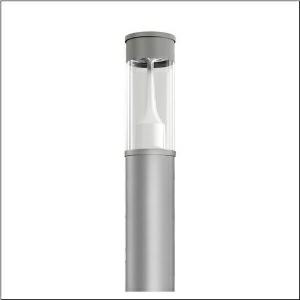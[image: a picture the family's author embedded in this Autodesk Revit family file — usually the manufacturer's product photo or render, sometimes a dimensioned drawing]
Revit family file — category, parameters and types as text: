
# Revit family: city-light_400_iq___p1_0a_5xa5305nf14hp_4342
name_source: partatom
category: Lighting Fixtures
units: mm (PartAtom-declared; Revit-internal decimal feet)

## family parameters
Cut with Voids When Loaded = No
Host = Face
Light Source = No
Part Type = Normal
Room Calculation Point = No
Round Connector Dimension = Use Diameter
Shared = No

## types (1)
- --- (1 x LED, 4210 lm, 33.6 W, 2700K)
    Apparent Load = 34 VA
    CIE Flux Codes = 31 62 91 95 100
    Color Rendering = 70
    Color Temperature = 2700K
    Default Elevation = 1800 mm
    Description = City-Light 400 iQ, light pillar, Module 540 iQ-SR, primary light control with 3 zone facetted reflector, of plastic, silver coated, highly specular, structured, primary optical cover: cover, of PMMA, transparent, partly coated, light distribution: P1.0a, primary light characteristic: strongly asymmetric, LED, High Power LED, rated luminous flux: 4.210lm, luminous efficacy: 125lm/W, light colour: 727, colour temperature: 2700K, control gear: iQ Street-Remote, control: pre-setting: logarithmic dimming characteristic, Street-Remote, Auto-Match, Temp-Guard, Lumen-Switch, Night-Set, Smart-Wire, Light-Fading, Desk-Remote (wireless, voltage-free reading and setting of iQ features in the workshop via application-optimized NFC function/RFID function), optimised constant luminous flux control (CLO 2.0), with terminal, 6-pole, max. 2.5mm², mains connection: 230..240V, AC, 50/60Hz, start of lifetime: 34W, end of service life: 36W, reduction: 15W, luminaire housing, cylindrical, of extruded aluminium section, coated, Siteco® metallic grey (DB 702S), length: 4.694mm, diameter: 200mm, Module 540 iQ-SR, traffic white (RAL 9016), equipment: Power, protection rating (complete): IP65, insulation class (complete): insulation class II (safety insulation), certification: CE, ENEC, VDE, packaging unit: 1 piece

Light Distribution: P1.0a
    Height = 500 mm
    Lamp = 1 x LED
    Lamp Light Flux = 4210 lm
    Lamp Power = 33.6 W
    Lamp count = 1
    Length = 200 mm  [stored 0.656168 ft]
    Luminous efficacy = 125 lm/W
    Manufacturer = Siteco
    ModVariant = No
    Model = 5XA5305NF14HP
    Mounting Place = Floor
    Mounting Type = Freestanding
    Number of Poles = 1
    OnlyDefault = Yes
    Power Factor = 1
    Product Name = City-Light 400 iQ | P1.0a
    Product group = light pillar
    ProductGroupID = 1301
    Protection Class = Protection class II
    Protection Degree = IP 65
    RLX_Detail_Level = 1
    RLX_Emergency_Light_Flux = 0 lm
    RLX_Emergency_Type = 0
    RLX_Emergency_Type_DB = No
    RlxData = <blob elided: 53521 chars, md5=2d689ea6>
    Socket = socket
    Standby Power = 0 W
    System Light Flux = 4210 lm
    System Power = 34 W
    Type Comments = factory setting: luminous flux: 100 % | dim-lin: 254 | 695 mA
    Type Image = l_1006916.jpg
    URL = http://relux.com
    VarID = @adj_173945
    Voltage = 0 V
    Weight = 0.00 kg
    Width = 0 mm  [stored 0 ft]

note: [stored X ft] marks values corroborated as IEEE doubles in the binary element streams (Revit-internal decimal feet)

## geometry (parser evidence)
native form markers: Blend x4, Sweep x9
no freeform markers — native parametric forms only
